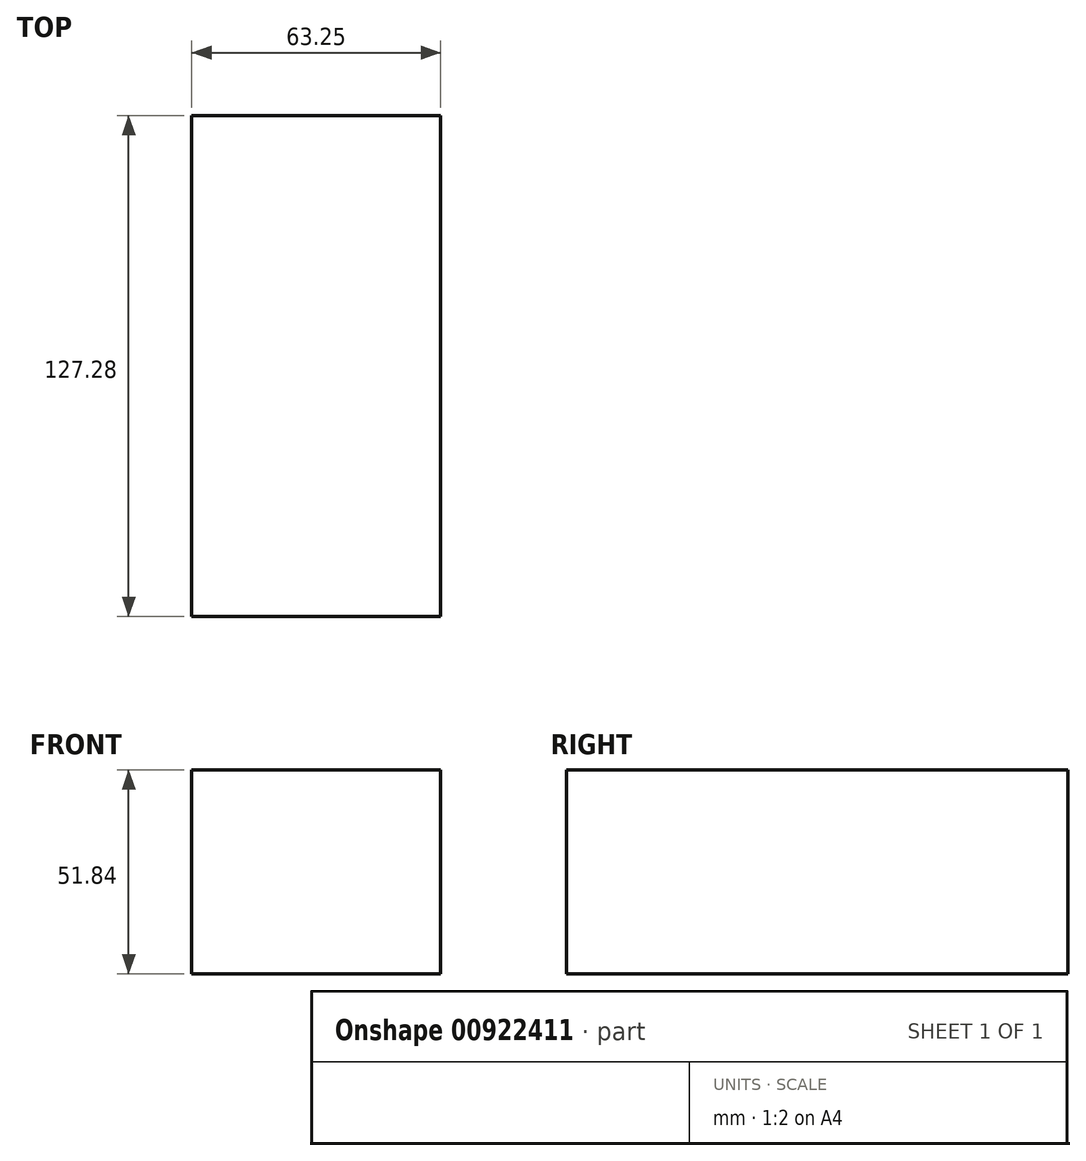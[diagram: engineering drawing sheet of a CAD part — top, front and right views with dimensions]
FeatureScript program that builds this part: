
annotation { "Feature Type Name" : "Feature", "Feature Type Description" : "" }
export const myFeature = defineFeature(function(context is Context, id is Id, definition is map)
    precondition{}
    {
        {
            var Q0;
            Q0=qCreatedBy(makeId("Right.planeOp"),FACE);
            var sketch = newSketch(context, id + "F0", { "sketchPlane" : qUnion([Q0])});
            skLineSegment(sketch, "E0.bottom", {"start": v(-74.7, 39.54) * mm, "end": v(52.58, 39.54) * mm});
            skLineSegment(sketch, "E0.top", {"start": v(-74.7, -12.3) * mm, "end": v(52.58, -12.3) * mm});
            skLineSegment(sketch, "E0.left", {"start": v(-74.7, 39.54) * mm, "end": v(-74.7, -12.3) * mm});
            skLineSegment(sketch, "E0.right", {"start": v(52.58, 39.54) * mm, "end": v(52.58, -12.3) * mm});
            skSolve(sketch);
        }
        {
            var Q0;
            Q0=makeQuery(id+"F0.imprint","IMPRINT",FACE,{"disambiguationData":[TD([[makeQuery(id+"F0.imprint","IMPRINT",EDGE,{"derivedFrom":sQuery(id+"F0.wireOp",EDGE,"E0.bottom")}),-1.0]])]});
            extrude(context, id + "F1", {"entities" : qUnion([Q0]), "depth" : 63.25 * mm, "offsetDistance" : 25.4 * mm});
        }
    });
